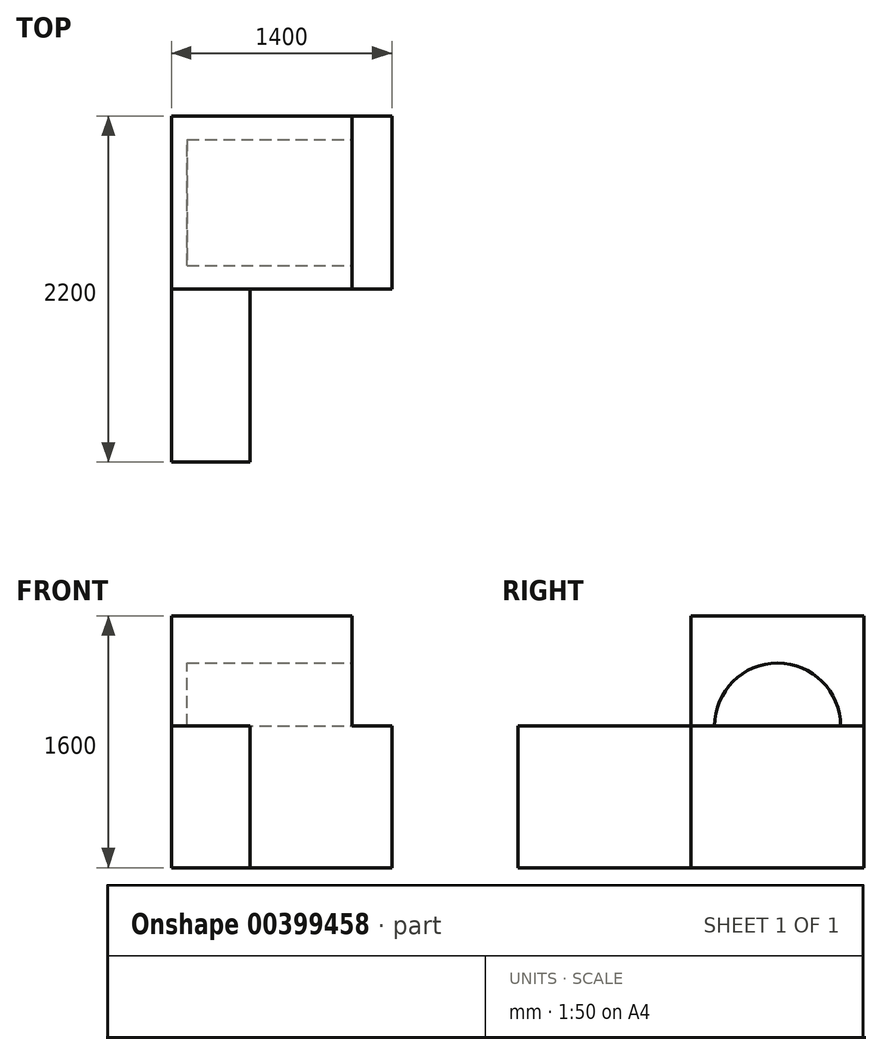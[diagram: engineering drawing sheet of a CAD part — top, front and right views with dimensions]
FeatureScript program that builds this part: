
annotation { "Feature Type Name" : "Feature", "Feature Type Description" : "" }
export const myFeature = defineFeature(function(context is Context, id is Id, definition is map)
    precondition{}
    {
        {
            var Q0;
            Q0=qCreatedBy(makeId("Top.planeOp"),FACE);
            cPlane(context, id + "F0", {"entities" : qUnion([Q0]), "cplaneType" : CPlaneType.OFFSET, "offset" : 150 * mm, "width" : 152.4 * mm, "height" : 152.4 * mm});
        }
        {
            var Q0;
            Q0=qCreatedBy(id+"F0.planeOp",FACE);
            var sketch = newSketch(context, id + "F1", { "sketchPlane" : qUnion([Q0])});
            skLineSegment(sketch, "E0", {"start": v(0, 0) * mm, "end": v(0, -2200) * mm});
            skLineSegment(sketch, "E1", {"start": v(0, -2200) * mm, "end": v(500, -2200) * mm});
            skLineSegment(sketch, "E2", {"start": v(500, -2200) * mm, "end": v(500, -1100) * mm});
            skLineSegment(sketch, "E3", {"start": v(500, -1100) * mm, "end": v(1400, -1100) * mm});
            skLineSegment(sketch, "E4", {"start": v(1400, -1100) * mm, "end": v(1400, 0) * mm});
            skLineSegment(sketch, "E5", {"start": v(1400, 0) * mm, "end": v(0, 0) * mm});
            skSolve(sketch);
        }
        {
            var Q0;
            Q0 = qSketchRegion(id + "F1", true);
            extrude(context, id + "F2", {"entities" : qUnion([Q0]), "depth" : 900 * mm});
        }
        {
            var Q0;
            Q0=makeQuery(id+"F2.opExtrude","CAP_FACE",FACE,{"disambiguationData":[OSD([sQuery(id+"F1.wireOp",EDGE,"E0"),sQuery(id+"F1.wireOp",EDGE,"E1"),sQuery(id+"F1.wireOp",EDGE,"E2"),sQuery(id+"F1.wireOp",EDGE,"E3"),sQuery(id+"F1.wireOp",EDGE,"E4"),sQuery(id+"F1.wireOp",EDGE,"E5")])],"isStart":false});
            cPlane(context, id + "F3", {"entities" : qUnion([Q0]), "cplaneType" : CPlaneType.OFFSET, "offset" : 0 * mm, "width" : 150 * mm, "height" : 150 * mm});
        }
        {
            var Q0;
            Q0=qCreatedBy(id+"F3.planeOp",FACE);
            var sketch = newSketch(context, id + "F4", { "sketchPlane" : qUnion([Q0])});
            skLineSegment(sketch, "E6.bottom", {"start": v(0, 0) * mm, "end": v(1148.55, 0) * mm});
            skLineSegment(sketch, "E6.top", {"start": v(0, -1100) * mm, "end": v(1148.55, -1100) * mm});
            skLineSegment(sketch, "E6.left", {"start": v(0, 0) * mm, "end": v(0, -1100) * mm});
            skLineSegment(sketch, "E6.right", {"start": v(1148.55, 0) * mm, "end": v(1148.55, -1100) * mm});
            skSolve(sketch);
        }
        {
            var Q0;
            Q0=makeQuery(id+"F4.imprint","IMPRINT",FACE,{"disambiguationData":[TD([[makeQuery(id+"F4.imprint","IMPRINT",EDGE,{"derivedFrom":sQuery(id+"F4.wireOp",EDGE,"E6.bottom")}),-1.0]])]});
            extrude(context, id + "F5", {"entities" : qUnion([Q0]), "operationType" : NewBodyOperationType.ADD, "depth" : 700 * mm});
        }
        {
            var Q0;
            Q0=makeQuery(id+"F5.boolean.opBoolean","MERGE",FACE,{"derivedFrom":[makeQuery(id+"F2.opExtrude","SWEPT_FACE",FACE,{"disambiguationData":[OSD([sQuery(id+"F1.wireOp",EDGE,"E0")])]}),makeQuery(id+"F5.opExtrude","SWEPT_FACE",FACE,{"disambiguationData":[OSD([sQuery(id+"F4.wireOp",EDGE,"E6.left")])]})]});
            cPlane(context, id + "F6", {"entities" : qUnion([Q0]), "cplaneType" : CPlaneType.OFFSET, "offset" : 100 * mm, "oppositeDirection" : true, "width" : 150 * mm, "height" : 150 * mm});
        }
        {
            var Q0;
            Q0=makeQuery(id+"F5.opExtrude","SWEPT_FACE",FACE,{"disambiguationData":[OSD([sQuery(id+"F4.wireOp",EDGE,"E6.right")])]});
            var sketch = newSketch(context, id + "F7", { "sketchPlane" : qUnion([Q0])});
            skArc(sketch, "E7", {"start": v(-150, 1050) * mm, "mid": v(-550, 1450) * mm, "end": v(-950, 1050) * mm});
            skLineSegment(sketch, "E8", {"start": v(-150, 1050) * mm, "end": v(-950, 1050) * mm});
            skSolve(sketch);
        }
        {
            var Q0;
            Q0=makeQuery(id+"F7.imprint","IMPRINT",FACE,{"disambiguationData":[TD([[makeQuery(id+"F7.imprint","IMPRINT",EDGE,{"derivedFrom":sQuery(id+"F7.wireOp",EDGE,"E7")}),1.0]])]});
            var Q1;
            Q1=qCreatedBy(id+"F6.planeOp",FACE);
            extrude(context, id + "F8", {"entities" : qUnion([Q0]), "operationType" : NewBodyOperationType.REMOVE, "endBound" : BoundingType.UP_TO_SURFACE, "oppositeDirection" : true, "endBoundEntityFace" : qUnion([Q1]), "depth" : 25 * mm});
        }
    });
